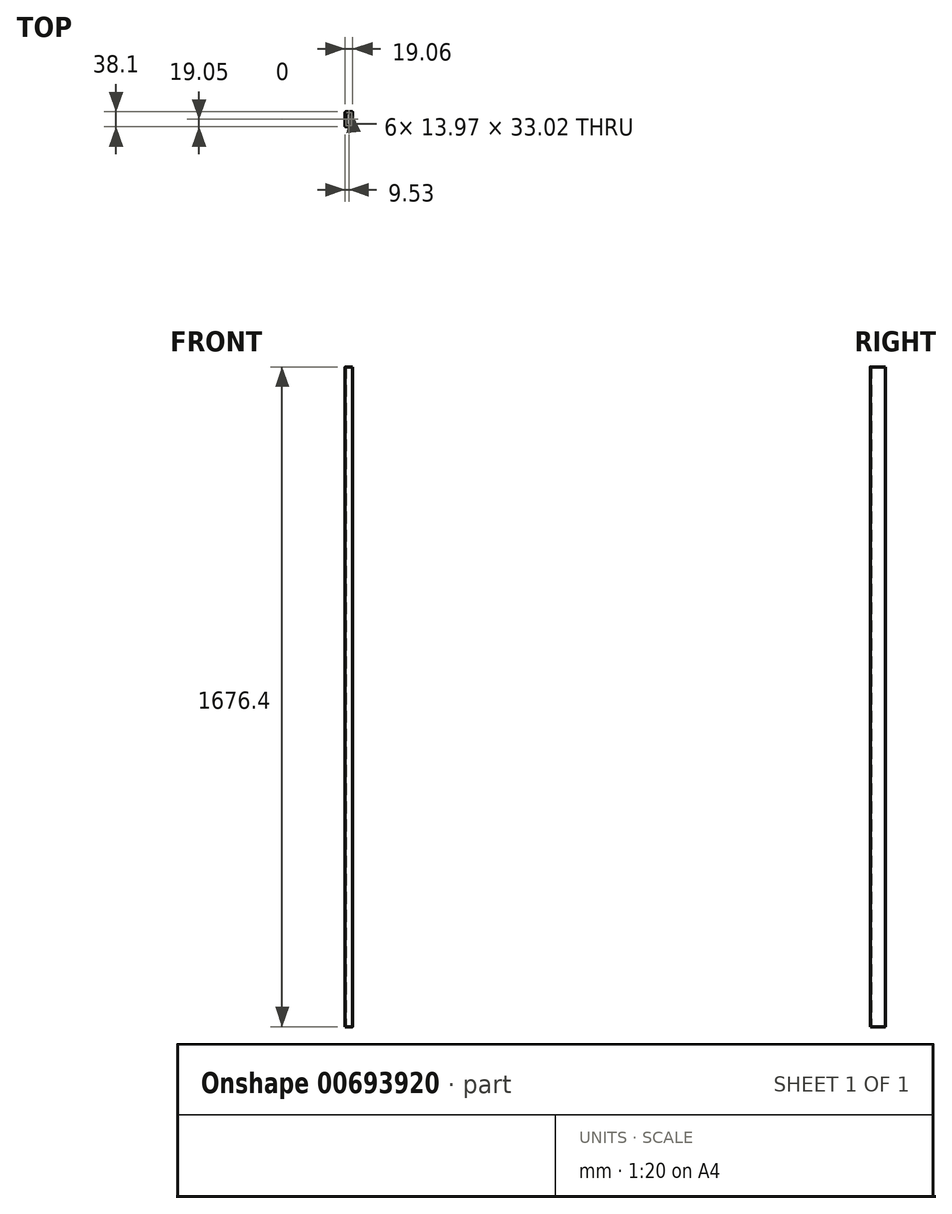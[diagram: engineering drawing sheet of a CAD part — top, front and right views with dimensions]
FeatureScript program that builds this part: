
annotation { "Feature Type Name" : "Feature", "Feature Type Description" : "" }
export const myFeature = defineFeature(function(context is Context, id is Id, definition is map)
    precondition{}
    {
        {
            var Q0;
            Q0=qCreatedBy(makeId("Top.planeOp"),FACE);
            var sketch = newSketch(context, id + "F0", { "sketchPlane" : qUnion([Q0])});
            skLineSegment(sketch, "E0.bottom", {"start": v(-8.02, 19.05) * mm, "end": v(8.03, 19.05) * mm});
            skLineSegment(sketch, "E0.top", {"start": v(-8.02, -19.05) * mm, "end": v(8.03, -19.05) * mm});
            skLineSegment(sketch, "E0.left", {"start": v(-9.53, 17.55) * mm, "end": v(-9.53, -17.55) * mm});
            skLineSegment(sketch, "E0.right", {"start": v(9.53, 17.55) * mm, "end": v(9.52, -17.55) * mm});
            skPoint(sketch, "E0.middle", {"position": v(0, 0) * mm});
            skPoint(sketch, "E1.visualSharp", {"position": v(-9.52, 19.05) * mm});
            skArc(sketch, "E1.filletArc", {"start": v(-8.02, 19.05) * mm, "mid": v(-9.09, 18.61) * mm, "end": v(-9.52, 17.55) * mm});
            skPoint(sketch, "E2.visualSharp", {"position": v(9.53, 19.05) * mm});
            skArc(sketch, "E2.filletArc", {"start": v(9.53, 17.55) * mm, "mid": v(9.09, 18.61) * mm, "end": v(8.03, 19.05) * mm});
            skPoint(sketch, "E3.visualSharp", {"position": v(9.52, -19.05) * mm});
            skArc(sketch, "E3.filletArc", {"start": v(8.03, -19.05) * mm, "mid": v(9.09, -18.61) * mm, "end": v(9.53, -17.55) * mm});
            skPoint(sketch, "E4.visualSharp", {"position": v(-9.53, -19.05) * mm});
            skArc(sketch, "E4.filletArc", {"start": v(-9.52, -17.55) * mm, "mid": v(-9.09, -18.61) * mm, "end": v(-8.02, -19.05) * mm});
            skLineSegment(sketch, "E5.0", {"start": v(-6.98, 16.5) * mm, "end": v(6.99, 16.5) * mm});
            skLineSegment(sketch, "E5.1", {"start": v(-6.98, 16.5) * mm, "end": v(-6.99, -16.51) * mm});
            skLineSegment(sketch, "E5.2", {"start": v(-6.99, -16.51) * mm, "end": v(6.98, -16.51) * mm});
            skLineSegment(sketch, "E5.3", {"start": v(6.99, 16.5) * mm, "end": v(6.98, -16.51) * mm});
            skSolve(sketch);
        }
        {
            var Q0;
            Q0=makeQuery(id+"F0.imprint","IMPRINT",FACE,{"disambiguationData":[TD([[makeQuery(id+"F0.imprint","IMPRINT",EDGE,{"derivedFrom":sQuery(id+"F0.wireOp",EDGE,"E0.bottom")}),-1.0]])]});
            extrude(context, id + "F1", {"entities" : qUnion([Q0]), "depth" : 1676.4 * mm, "offsetDistance" : 25 * mm});
        }
    });
